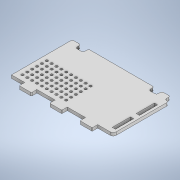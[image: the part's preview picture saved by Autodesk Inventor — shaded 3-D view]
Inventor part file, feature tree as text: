
AUTODESK INVENTOR PART (.ipt)
format: ipt  version: 2020 (Build 240168000, 168)  size: 301,568 bytes
history: native  units: mm
features: extrude x1, sketch x1
ambient origin geometry x8: Origin, YZ Plane, XZ Plane, XY Plane, X Axis, Y Axis, Z Axis, Center Point
bodies: Solid1 (feature_tree)
feature tree (2):
  extrude  "Extrusion1"  Depth=21.75mm
  sketch  "Sketch1"  dims[d1=100.0mm d2=21.75mm d3=20.0mm d4=30.0mm d5=20.0mm d6=30.0mm d7=20.0mm d8=9.0mm d9=1.0mm d14=108.0mm d15=14.0mm d19=9.0mm d24=12.7mm d25=167.25mm d26=3.0mm d27=3.0mm d28=3.0mm d29=12.7mm d30=6.0mm d31=3.0mm d32=5.0mm d33=4.25mm d34=5.25mm d35=30.0mm d36=9.5mm d37=8.0mm d38=4.0mm d39=100.0mm d41=8.0mm d42=60.0mm d44=8.0mm d47=9.0mm d48=9.0mm d49=5.0mm d50=0.0mm d51=91.0mm d52=0.872665mm]
